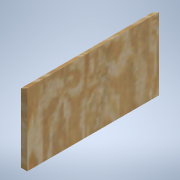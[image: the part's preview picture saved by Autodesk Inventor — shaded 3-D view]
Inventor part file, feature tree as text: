
AUTODESK INVENTOR PART (.ipt)
format: ipt  version: 2021.1 (Build 251245000, 245)  size: 123,392 bytes
history: native  units: in
note: dims shown in document units (in); Inventor stores cm internally (conversion verified against a paired STEP export)
features: reference x4, other x4, extrude x1, sketch x1
ambient origin geometry x8: Origin, YZ Plane, XZ Plane, XY Plane, X Axis, Y Axis, Z Axis, Center Point
bodies: Solid1 (feature_tree)
feature tree (10):
  extrude  "Extrusion1"  [1 undecoded]
  sketch  "Sketch1"  dims[d1=10.6299in d2=0.0in]
  reference  "Reference1"
  reference  "Reference2"
  reference  "Reference3"
  reference  "Reference4"
  other  "<userpath>\Documents\Kerbal Kontroller\Design\Final\Inventor\Final.iam"
  other  "Final.iam"
  other  "Sides:1"
  other  "Bottom:1"
note: 1 required parameter value undecoded (feature->parameter linkage not recoverable at this tier; creation-order binding heuristic only, values carry confidence <= 0.55)
